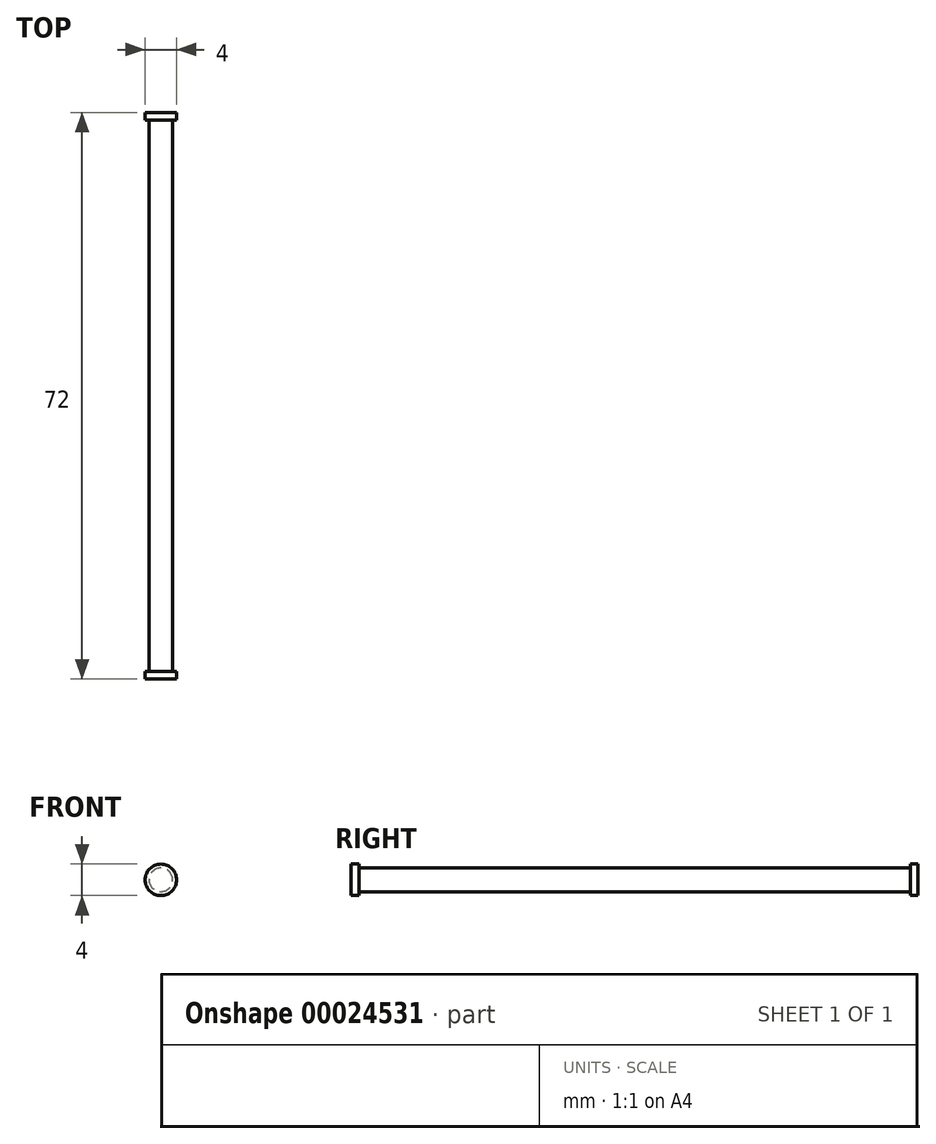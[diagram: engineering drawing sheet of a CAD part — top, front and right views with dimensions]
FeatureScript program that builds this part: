
annotation { "Feature Type Name" : "Feature", "Feature Type Description" : "" }
export const myFeature = defineFeature(function(context is Context, id is Id, definition is map)
    precondition{}
    {
        {
            var Q0;
            Q0=qCreatedBy(makeId("Front.planeOp"),FACE);
            var sketch = newSketch(context, id + "F0", { "sketchPlane" : qUnion([Q0])});
            skCircle(sketch, "E0", {"center": v(-80.87, -13.86) * mm, "radius": 1.5 * mm});
            skSolve(sketch);
        }
        {
            var Q0;
            Q0 = qSketchRegion(id + "F0", true);
            extrude(context, id + "F1", {"entities" : qUnion([Q0]), "depth" : 70 * mm});
        }
        {
            var Q0;
            Q0=makeQuery(id+"F1.opExtrude","CAP_FACE",FACE,{"disambiguationData":[OSD([sQuery(id+"F0.wireOp",EDGE,"E0")])],"isStart":true});
            var sketch = newSketch(context, id + "F2", { "sketchPlane" : qUnion([Q0])});
            skCircle(sketch, "E1", {"center": v(80.87, -13.86) * mm, "radius": 2 * mm});
            skSolve(sketch);
        }
        {
            var Q0;
            Q0 = qSketchRegion(id + "F2", true);
            extrude(context, id + "F3", {"entities" : qUnion([Q0]), "operationType" : NewBodyOperationType.ADD, "depth" : 1 * mm});
        }
        {
            var Q0;
            Q0=makeQuery(id+"F1.opExtrude","CAP_FACE",FACE,{"disambiguationData":[OSD([sQuery(id+"F0.wireOp",EDGE,"E0")])],"isStart":false});
            var sketch = newSketch(context, id + "F4", { "sketchPlane" : qUnion([Q0])});
            skCircle(sketch, "E2", {"center": v(-80.87, -13.86) * mm, "radius": 2 * mm});
            skSolve(sketch);
        }
        {
            var Q0;
            Q0 = qSketchRegion(id + "F4", true);
            extrude(context, id + "F5", {"entities" : qUnion([Q0]), "operationType" : NewBodyOperationType.ADD, "depth" : 1 * mm});
        }
    });
